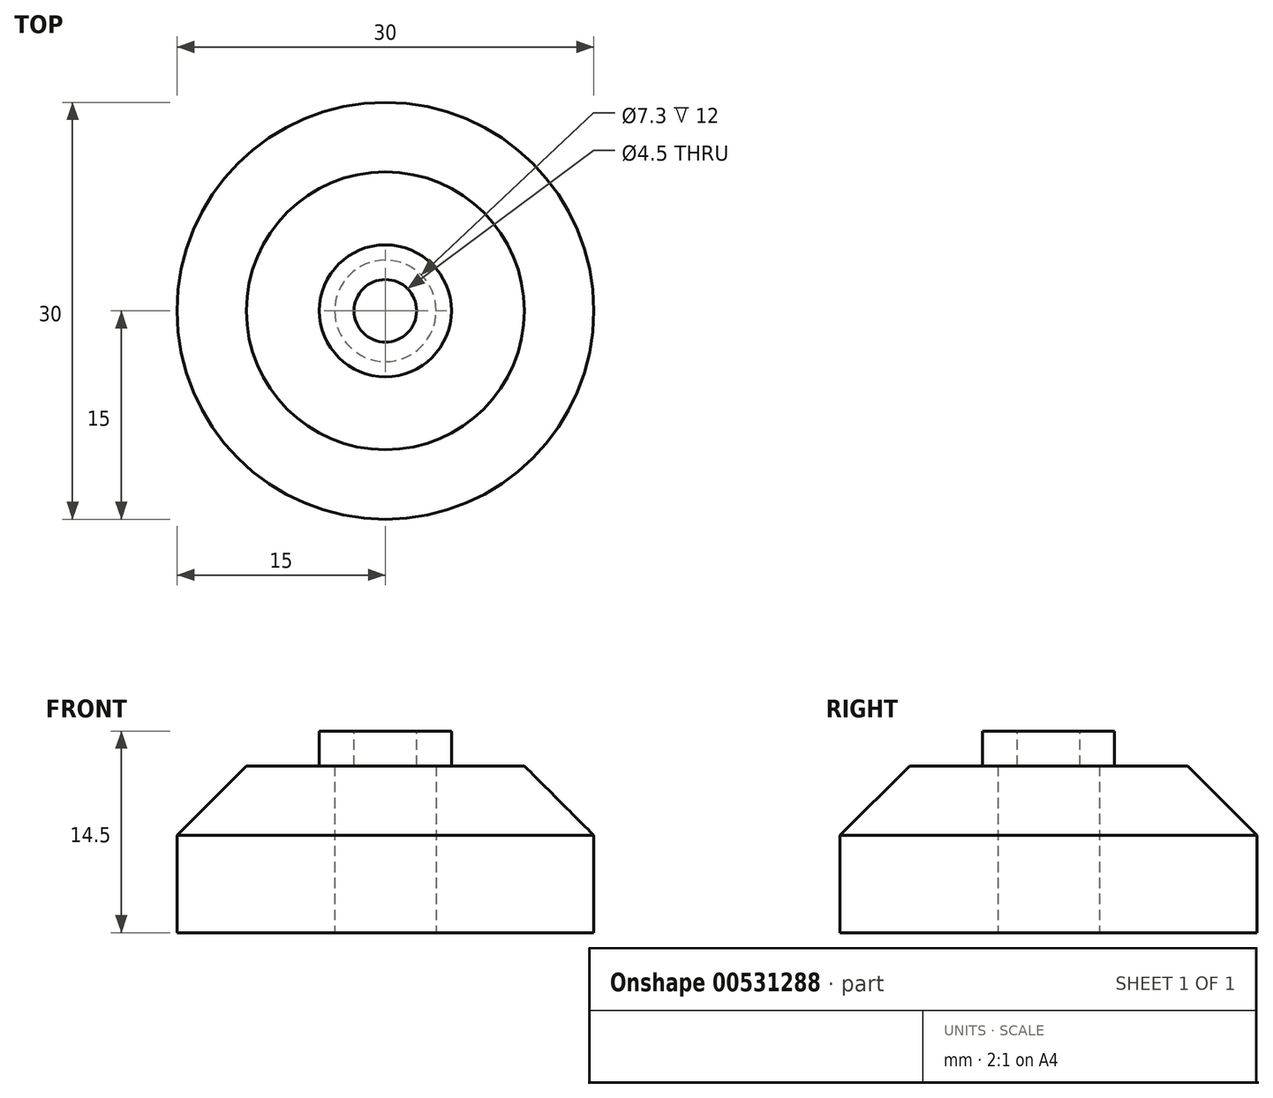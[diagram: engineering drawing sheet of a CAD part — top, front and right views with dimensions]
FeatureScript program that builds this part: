
annotation { "Feature Type Name" : "Feature", "Feature Type Description" : "" }
export const myFeature = defineFeature(function(context is Context, id is Id, definition is map)
    precondition{}
    {
        {
            var Q0;
            Q0=qCreatedBy(makeId("Top.planeOp"),FACE);
            var sketch = newSketch(context, id + "F0", { "sketchPlane" : qUnion([Q0])});
            skCircle(sketch, "E0", {"center": v(0, 0) * mm, "radius": 15 * mm});
            skCircle(sketch, "E1", {"center": v(0, 0) * mm, "radius": 3.65 * mm});
            skSolve(sketch);
        }
        {
            var Q0;
            Q0 = qSketchRegion(id + "F0", true);
            var Q1;
            Q1=sQuery(id+"F0.wireOp",EDGE,"E0");
            extrude(context, id + "F1", {"entities" : qUnion([Q0]), "surfaceEntities" : qUnion([Q1]), "depth" : 8 * mm, "offsetDistance" : 25 * mm});
        }
        {
            var Q0;
            Q0=makeQuery(id+"F1.opExtrude","CAP_FACE",FACE,{"disambiguationData":[OSD([sQuery(id+"F0.wireOp",EDGE,"E0")])],"isStart":false});
            var sketch = newSketch(context, id + "F2", { "sketchPlane" : qUnion([Q0])});
            skCircle(sketch, "E2", {"center": v(0, 0) * mm, "radius": 15 * mm});
            skSolve(sketch);
        }
        {
            var Q0;
            Q0 = qSketchRegion(id + "F2", true);
            extrude(context, id + "F3", {"entities" : qUnion([Q0]), "operationType" : NewBodyOperationType.ADD, "depth" : 4 * mm, "offsetDistance" : 25 * mm});
        }
        {
            var Q0;
            Q0=makeQuery(id+"F3.opExtrude","CAP_EDGE",EDGE,{"disambiguationData":[OSD([sQuery(id+"F2.wireOp",EDGE,"E2")])],"isStart":false});
            chamfer(context, id + "F4", {"entities" : qUnion([Q0]), "width" : 5 * mm, "tangentPropagation" : true});
        }
        {
            var Q0;
            Q0=makeQuery(id+"F3.opExtrude","CAP_FACE",FACE,{"disambiguationData":[OSD([sQuery(id+"F2.wireOp",EDGE,"E2")])],"isStart":false});
            var sketch = newSketch(context, id + "F5", { "sketchPlane" : qUnion([Q0])});
            skCircle(sketch, "E3", {"center": v(0, 0) * mm, "radius": 4.75 * mm});
            skSolve(sketch);
        }
        {
            var Q0;
            Q0=makeQuery(id+"F5.imprint","IMPRINT",FACE,{"disambiguationData":[TD([[makeQuery(id+"F5.imprint","IMPRINT",EDGE,{"derivedFrom":sQuery(id+"F5.wireOp",EDGE,"E3")}),1.0]])]});
            extrude(context, id + "F6", {"entities" : qUnion([Q0]), "operationType" : NewBodyOperationType.ADD, "depth" : 2.5 * mm, "offsetDistance" : 25 * mm});
        }
        {
            var Q0;
            Q0=makeQuery(id+"F6.opExtrude","CAP_FACE",FACE,{"disambiguationData":[OSD([sQuery(id+"F5.wireOp",EDGE,"E3")])],"isStart":false});
            var sketch = newSketch(context, id + "F7", { "sketchPlane" : qUnion([Q0])});
            skCircle(sketch, "E4", {"center": v(0, 0) * mm, "radius": 2.25 * mm});
            skSolve(sketch);
        }
        {
            var Q0;
            Q0=makeQuery(id+"F7.imprint","IMPRINT",FACE,{"disambiguationData":[TD([[makeQuery(id+"F7.imprint","IMPRINT",EDGE,{"derivedFrom":sQuery(id+"F7.wireOp",EDGE,"E4")}),1.0]])]});
            extrude(context, id + "F8", {"entities" : qUnion([Q0]), "operationType" : NewBodyOperationType.REMOVE, "oppositeDirection" : true, "depth" : 5 * mm, "offsetDistance" : 25 * mm});
        }
        {
            var Q0;
            Q0=makeQuery(id+"F0.imprint","IMPRINT",FACE,{"disambiguationData":[TD([[makeQuery(id+"F0.imprint","IMPRINT",EDGE,{"derivedFrom":sQuery(id+"F0.wireOp",EDGE,"E1")}),1.0]])]});
            extrude(context, id + "F9", {"entities" : qUnion([Q0]), "operationType" : NewBodyOperationType.REMOVE, "depth" : 12 * mm, "offsetDistance" : 25 * mm});
        }
    });
